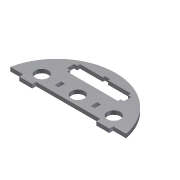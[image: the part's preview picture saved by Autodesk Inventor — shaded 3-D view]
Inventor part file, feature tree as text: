
AUTODESK INVENTOR PART (.ipt)
format: ipt  version: 2012 (Build 160160000, 160)  size: 140,800 bytes
history: native  units: mm
features: extrude x1, sketch x1
ambient origin geometry x8: Origin, YZ Plane, XZ Plane, XY Plane, X Axis, Y Axis, Z Axis, Center Point
feature tree (2):
  extrude  "Extrusion3"  Depth=46.0mm
  sketch  "Sketch1"  dims[d1=6.0mm d6=9.0mm d7=46.0mm d8=50.0mm d9=10.0mm d10=10.0mm d12=5.6mm d13=2.2mm d14=4.0mm d15=39.5mm d17=5.6mm d18=2.2mm d22=17.75mm d23=44.4mm d24=39.5mm d25=2.2mm d26=2.2mm d27=2.45mm d28=2.45mm d29=11.6mm d30=22.2mm d31=28.0mm d34=5.0mm d35=3.0mm d36=5.0mm d37=3.0mm d38=5.0mm d39=5.0mm d40=25.0mm d41=12.5mm d44=10.0mm d45=10.0mm d46=10.0mm d47=12.5mm d48=12.5mm d49=12.5mm d50=3.0mm d51=0.0mm]
